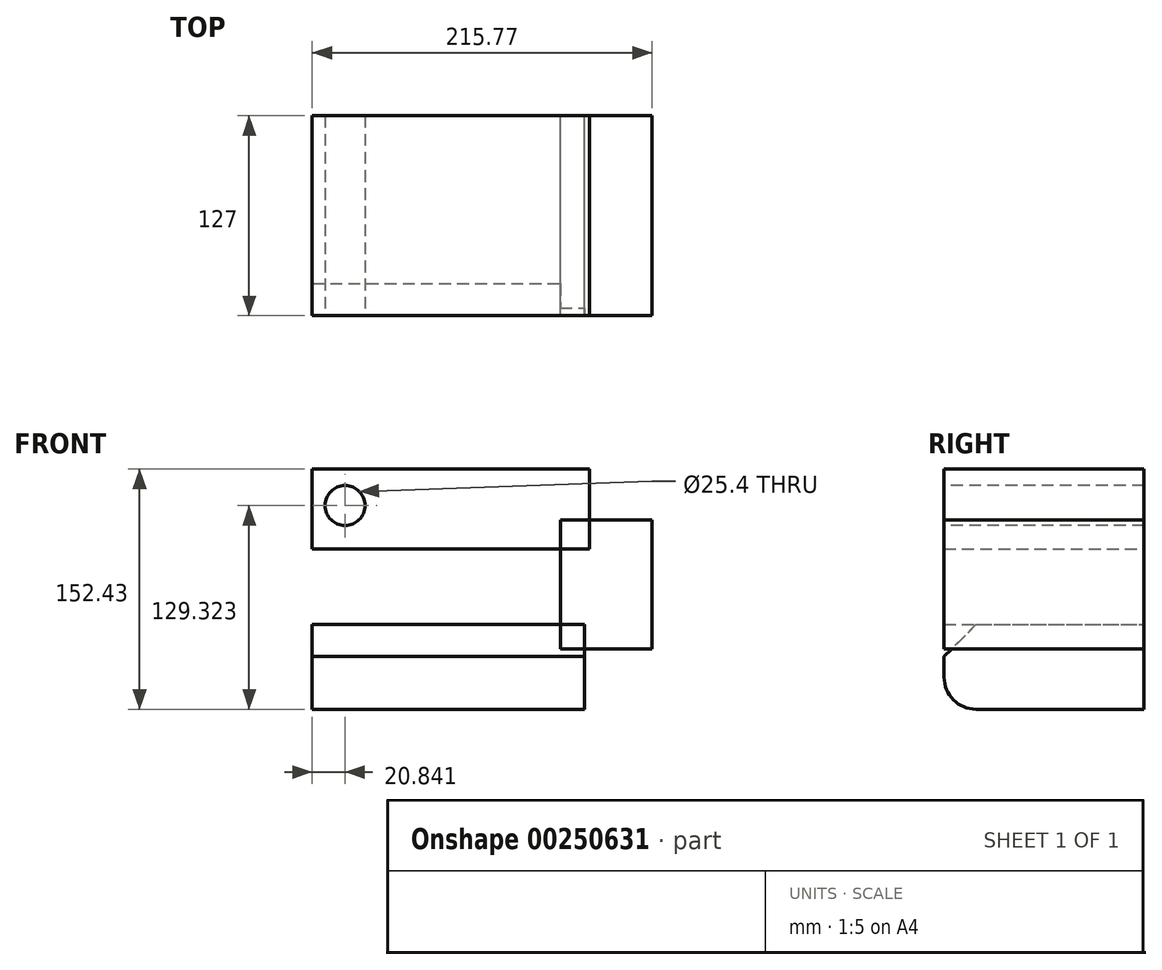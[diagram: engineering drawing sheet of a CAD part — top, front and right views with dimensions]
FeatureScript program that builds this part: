
annotation { "Feature Type Name" : "Feature", "Feature Type Description" : "" }
export const myFeature = defineFeature(function(context is Context, id is Id, definition is map)
    precondition{}
    {
        {
            var Q0;
            Q0=qCreatedBy(makeId("Front.planeOp"),FACE);
            var sketch = newSketch(context, id + "F0", { "sketchPlane" : qUnion([Q0])});
            skLineSegment(sketch, "E0.bottom", {"start": v(-28.93, 42.65) * mm, "end": v(29.25, 42.65) * mm});
            skLineSegment(sketch, "E0.top", {"start": v(-28.93, -39.1) * mm, "end": v(29.25, -39.1) * mm});
            skLineSegment(sketch, "E0.left", {"start": v(-28.93, 42.65) * mm, "end": v(-28.93, -39.1) * mm});
            skLineSegment(sketch, "E0.right", {"start": v(29.25, 42.65) * mm, "end": v(29.25, -39.1) * mm});
            skLineSegment(sketch, "E1.bottom", {"start": v(-10.52, 24.24) * mm, "end": v(-186.52, 24.24) * mm});
            skLineSegment(sketch, "E1.top", {"start": v(-10.52, 75.05) * mm, "end": v(-186.52, 75.05) * mm});
            skLineSegment(sketch, "E1.left", {"start": v(-10.52, 24.24) * mm, "end": v(-10.52, 75.05) * mm});
            skLineSegment(sketch, "E1.right", {"start": v(-186.52, 24.24) * mm, "end": v(-186.52, 75.05) * mm});
            skLineSegment(sketch, "E2.bottom", {"start": v(-13.46, -23.63) * mm, "end": v(-186.52, -23.63) * mm});
            skLineSegment(sketch, "E2.top", {"start": v(-13.46, -77.38) * mm, "end": v(-186.52, -77.38) * mm});
            skLineSegment(sketch, "E2.left", {"start": v(-13.46, -23.63) * mm, "end": v(-13.46, -77.38) * mm});
            skLineSegment(sketch, "E2.right", {"start": v(-186.52, -23.63) * mm, "end": v(-186.52, -77.38) * mm});
            skSolve(sketch);
        }
        {
            var Q0;
            {var subQ5=sQuery(id+"F0.wireOp",EDGE,"E1.top");Q0=makeQuery(id+"F0.imprint","IMPRINT",FACE,{"disambiguationData":[TD([[makeQuery(id+"F0.imprint","IMPRINT",EDGE,{"derivedFrom":subQ5}),1.0]])]});}
            var Q1;
            {var subQ0=sQuery(id+"F0.wireOp",EDGE,"E0.right");Q1=makeQuery(id+"F0.imprint","IMPRINT",FACE,{"disambiguationData":[TD([[makeQuery(id+"F0.imprint","IMPRINT",EDGE,{"derivedFrom":subQ0}),-1.0]])]});}
            var Q2;
            {var subQ7=sQuery(id+"F0.wireOp",EDGE,"E2.top");Q2=makeQuery(id+"F0.imprint","IMPRINT",FACE,{"disambiguationData":[TD([[makeQuery(id+"F0.imprint","IMPRINT",EDGE,{"derivedFrom":subQ7}),-1.0]])]});}
            extrude(context, id + "F1", {"entities" : qUnion([Q0, Q1, Q2]), "depth" : 127 * mm});
        }
        {
            var Q0;
            Q0=makeQuery(id+"F1.opExtrude","CAP_FACE",FACE,{"disambiguationData":[OSD([sQuery(id+"F0.wireOp",EDGE,"E0.bottom"),sQuery(id+"F0.wireOp",EDGE,"E0.left"),sQuery(id+"F0.wireOp",EDGE,"E1.bottom"),sQuery(id+"F0.wireOp",EDGE,"E1.top"),sQuery(id+"F0.wireOp",EDGE,"E1.left"),sQuery(id+"F0.wireOp",EDGE,"E1.right")])],"isStart":false});
            var sketch = newSketch(context, id + "F2", { "sketchPlane" : qUnion([Q0])});
            skLineSegment(sketch, "E3.bottom", {"start": v(-165.68, 51.94) * mm, "end": v(-110.83, 51.94) * mm});
            skLineSegment(sketch, "E3.top", {"start": v(-165.68, 64.94) * mm, "end": v(-110.83, 64.94) * mm});
            skLineSegment(sketch, "E3.left", {"start": v(-165.68, 51.94) * mm, "end": v(-165.68, 64.94) * mm});
            skLineSegment(sketch, "E3.right", {"start": v(-110.83, 51.94) * mm, "end": v(-110.83, 64.94) * mm});
            skSolve(sketch);
        }
        {
            var Q0;
            Q0=sQuery(id+"F2.wireOp",VERTEX,"E3.bottom.start");
            var Q1;
            Q1=makeQuery(id+"F1.opExtrude","SWEPT_BODY",BODY,{"disambiguationData":[OSD([sQuery(id+"F0.wireOp",EDGE,"E0.bottom"),sQuery(id+"F0.wireOp",EDGE,"E0.left"),sQuery(id+"F0.wireOp",EDGE,"E1.bottom"),sQuery(id+"F0.wireOp",EDGE,"E1.top"),sQuery(id+"F0.wireOp",EDGE,"E1.left"),sQuery(id+"F0.wireOp",EDGE,"E1.right")])]});
            hole(context, id + "F3", {"style" : HoleStyle.C_SINK, "endStyle" : HoleEndStyle.THROUGH, "holeDiameter" : 25.4 * mm, "cSinkDiameter" : 25.4 * mm, "cSinkAngle" : 45 * degree, "tappedDepth" : 12.7 * mm, "tapClearance" : 3, "locations" : qUnion([Q0]), "scope" : qUnion([Q1])});
        }
        {
            var Q0;
            {var subQ0=sQuery(id+"F0.wireOp",EDGE,"E2.bottom");Q0=makeQuery(id+"F1.opExtrude","CAP_EDGE",EDGE,{"disambiguationData":[OSD([subQ0]),TDD([makeQuery(id+"F0.imprint","IMPRINT",EDGE,{"disambiguationData":[TD([[makeQuery(id+"F0.imprint","INTERSECT",VERTEX,{"derivedFrom":[subQ0,sQuery(id+"F0.wireOp",EDGE,"E2.right")]}),1.0]])],"derivedFrom":subQ0})])],"isStart":false});}
            chamfer(context, id + "F4", {"entities" : qUnion([Q0]), "width" : 20.32 * mm, "tangentPropagation" : true});
        }
        {
            var Q0;
            Q0=makeQuery(id+"F1.opExtrude","CAP_EDGE",EDGE,{"disambiguationData":[OSD([sQuery(id+"F0.wireOp",EDGE,"E2.top")])],"isStart":false});
            fillet(context, id + "F5", {"entities" : qUnion([Q0]), "radius" : 20.32 * mm, "tangentPropagation" : true, "allowEdgeOverflow" : false});
        }
    });
